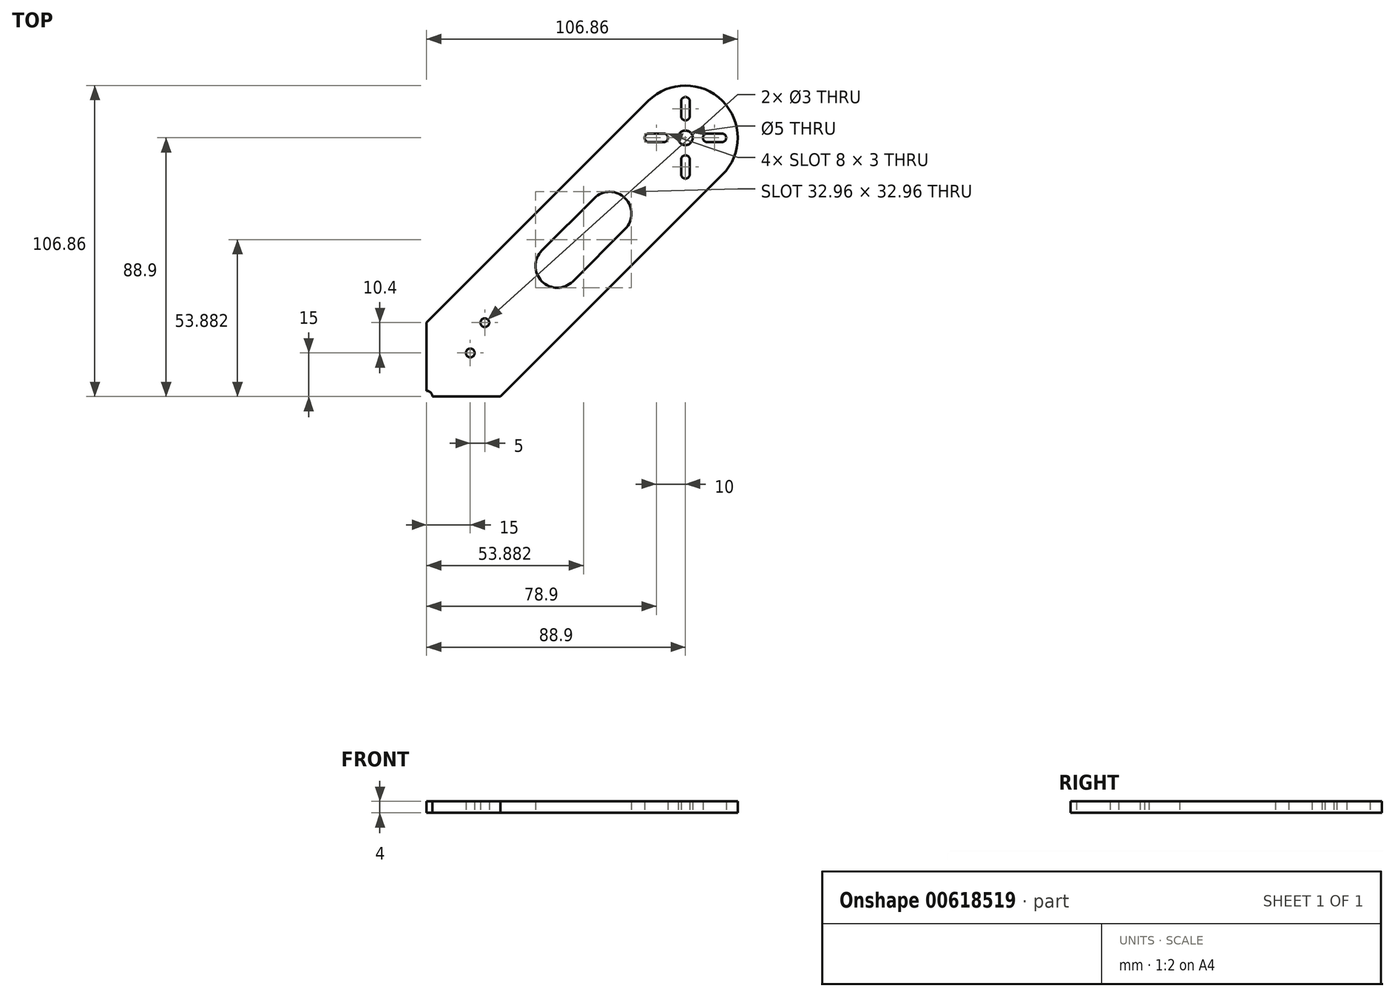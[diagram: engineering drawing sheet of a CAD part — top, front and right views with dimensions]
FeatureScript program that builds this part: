
annotation { "Feature Type Name" : "Feature", "Feature Type Description" : "" }
export const myFeature = defineFeature(function(context is Context, id is Id, definition is map)
    precondition{}
    {
        {
            var Q0;
            Q0=qCreatedBy(makeId("Top.planeOp"),FACE);
            var sketch = newSketch(context, id + "F0", { "sketchPlane" : qUnion([Q0])});
            skPoint(sketch, "E0.middle", {"position": v(0, 0) * mm});
            skLineSegment(sketch, "E1", {"start": v(0, 25.4) * mm, "end": v(76.2, 101.6) * mm});
            skLineSegment(sketch, "E2", {"start": v(25.4, 0) * mm, "end": v(101.6, 76.2) * mm});
            skArc(sketch, "E3", {"start": v(76.2, 101.6) * mm, "mid": v(101.6, 101.6) * mm, "end": v(101.6, 76.2) * mm});
            skPoint(sketch, "E4", {"position": v(88.9, 101.4) * mm});
            skPoint(sketch, "E5", {"position": v(101.4, 88.9) * mm});
            skPoint(sketch, "E6", {"position": v(88.9, 76.4) * mm});
            skPoint(sketch, "E7", {"position": v(76.4, 88.9) * mm});
            skPoint(sketch, "E8", {"position": v(96.4, 88.9) * mm});
            skPoint(sketch, "E9", {"position": v(88.9, 81.4) * mm});
            skPoint(sketch, "E10", {"position": v(81.4, 88.9) * mm});
            skCircle(sketch, "E11", {"center": v(88.9, 88.9) * mm, "radius": 2.5 * mm});
            skArc(sketch, "E12.0.startCap", {"start": v(87.4, 101.4) * mm, "mid": v(88.9, 102.9) * mm, "end": v(90.4, 101.4) * mm});
            skArc(sketch, "E12.0.endCap", {"start": v(90.4, 96.4) * mm, "mid": v(88.9, 94.9) * mm, "end": v(87.4, 96.4) * mm});
            skLineSegment(sketch, "E12.0.left", {"start": v(90.4, 101.4) * mm, "end": v(90.4, 96.4) * mm});
            skLineSegment(sketch, "E12.0.right", {"start": v(87.4, 101.4) * mm, "end": v(87.4, 96.4) * mm});
            skLineSegment(sketch, "E13.1.1", {"start": v(76.4, 87.4) * mm, "end": v(81.4, 87.4) * mm});
            skArc(sketch, "E13.1.2", {"start": v(76.4, 87.4) * mm, "mid": v(74.9, 88.9) * mm, "end": v(76.4, 90.4) * mm});
            skArc(sketch, "E13.1.3", {"start": v(81.4, 90.4) * mm, "mid": v(82.9, 88.9) * mm, "end": v(81.4, 87.4) * mm});
            skLineSegment(sketch, "E13.1.4", {"start": v(76.4, 90.4) * mm, "end": v(81.4, 90.4) * mm});
            skLineSegment(sketch, "E13.2.1", {"start": v(90.4, 76.4) * mm, "end": v(90.4, 81.4) * mm});
            skArc(sketch, "E13.2.2", {"start": v(90.4, 76.4) * mm, "mid": v(88.9, 74.9) * mm, "end": v(87.4, 76.4) * mm});
            skArc(sketch, "E13.2.3", {"start": v(87.4, 81.4) * mm, "mid": v(88.9, 82.9) * mm, "end": v(90.4, 81.4) * mm});
            skLineSegment(sketch, "E13.2.4", {"start": v(87.4, 76.4) * mm, "end": v(87.4, 81.4) * mm});
            skLineSegment(sketch, "E13.3.1", {"start": v(101.4, 90.4) * mm, "end": v(96.4, 90.4) * mm});
            skArc(sketch, "E13.3.2", {"start": v(101.4, 90.4) * mm, "mid": v(102.9, 88.9) * mm, "end": v(101.4, 87.4) * mm});
            skArc(sketch, "E13.3.3", {"start": v(96.4, 87.4) * mm, "mid": v(94.9, 88.9) * mm, "end": v(96.4, 90.4) * mm});
            skLineSegment(sketch, "E13.3.4", {"start": v(101.4, 87.4) * mm, "end": v(96.4, 87.4) * mm});
            skPoint(sketch, "E14", {"position": v(44.9, 44.9) * mm});
            skArc(sketch, "E15.0.startCap", {"start": v(50.2, 39.6) * mm, "mid": v(39.6, 39.6) * mm, "end": v(39.6, 50.2) * mm});
            skArc(sketch, "E15.0.endCap", {"start": v(57.56, 68.17) * mm, "mid": v(68.17, 68.17) * mm, "end": v(68.17, 57.56) * mm});
            skLineSegment(sketch, "E15.0.left", {"start": v(39.6, 50.2) * mm, "end": v(57.56, 68.17) * mm});
            skLineSegment(sketch, "E15.0.right", {"start": v(50.2, 39.6) * mm, "end": v(68.17, 57.56) * mm});
            skArc(sketch, "E16", {"start": v(0, 2) * mm, "mid": v(1.41, 1.41) * mm, "end": v(2, 0) * mm});
            skCircle(sketch, "E17", {"center": v(20, 25.4) * mm, "radius": 1.5 * mm});
            skCircle(sketch, "E18", {"center": v(15, 15) * mm, "radius": 1.5 * mm});
            skLineSegment(sketch, "E19", {"start": v(0, 25.4) * mm, "end": v(0, 2) * mm});
            skLineSegment(sketch, "E20", {"start": v(2, 0) * mm, "end": v(25.4, 0) * mm});
            skSolve(sketch);
        }
        {
            var Q0;
            Q0=makeQuery(id+"F0.imprint","IMPRINT",FACE,{"disambiguationData":[TD([[makeQuery(id+"F0.imprint","IMPRINT",EDGE,{"derivedFrom":sQuery(id+"F0.wireOp",EDGE,"E1")}),-1.0]])]});
            extrude(context, id + "F1", {"entities" : qUnion([Q0]), "depth" : 4 * mm, "offsetDistance" : 25 * mm});
        }
    });
